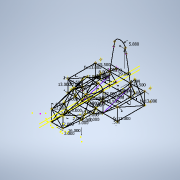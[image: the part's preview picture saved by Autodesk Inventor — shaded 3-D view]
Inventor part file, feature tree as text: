
AUTODESK INVENTOR PART (.ipt)
format: ipt  version: 2021 (Build 250183000, 183)  size: 271,872 bytes
history: native  units: in
note: dims shown in document units (in); Inventor stores cm internally (conversion verified against a paired STEP export)
features: other x52, plane x41, sketch x29
ambient origin geometry x8: Origin, YZ Plane, XZ Plane, XY Plane, X Axis, Y Axis, Z Axis, Center Point
feature tree (122):
  sketch  "Sketch1"  dims[d0=12.0in]
  plane  "Work Plane1"
  sketch  "Sketch2"  dims[d1=12.0in]
  plane  "Work Plane2"
  plane  "Work Plane3"
  sketch  "Sketch3"  dims[d2=2.0in]
  plane  "Work Plane4"
  sketch  "Sketch4"  dims[d3=-18.5in]
  plane  "Work Plane5"
  plane  "Work Plane6"
  plane  "Work Plane7"
  plane  "Work Plane8"
  plane  "Work Plane9"
  other  "Work Point1"
  other  "Work Point2"
  other  "Work Point3"
  other  "Work Point4"
  other  "Work Point5"
  other  "Work Point6"
  other  "Work Point7"
  other  "Work Point8"
  other  "Work Point9"
  other  "Work Point10"
  other  "Work Point11"
  other  "Work Point12"
  other  "Work Point13"
  other  "Work Point14"
  other  "Work Point15"
  other  "Work Point16"
  other  "Work Point17"
  other  "Work Point18"
  other  "Work Point19"
  other  "Work Point20"
  other  "Work Point21"
  other  "Work Point22"
  other  "Work Point23"
  other  "Work Point24"
  other  "Work Point25"
  other  "Work Point26"
  other  "Work Point27"
  other  "Work Point28"
  other  "Work Point29"
  other  "Work Point30"
  other  "Work Point31"
  other  "Work Point32"
  other  "Work Point33"
  other  "Work Point34"
  other  "Work Point35"
  other  "Work Point36"
  other  "Work Point37"
  other  "Work Point38"
  other  "Work Point39"
  other  "Work Point40"
  other  "Work Point41"
  other  "Work Point42"
  other  "Work Point43"
  other  "Work Point44"
  plane  "Work Plane10"
  sketch  "Sketch11"  dims[d4=16.0in]
  plane  "Work Plane11"
  sketch  "Sketch12"  dims[d5=2.0in]
  plane  "Work Plane12"
  sketch  "Sketch13"  dims[d6=3.0in]
  plane  "Work Plane13"
  sketch  "Sketch14"  dims[d7=6.0in]
  plane  "Work Plane14"
  sketch  "Sketch15"  dims[d8=3.0in]
  plane  "Work Plane15"
  sketch  "Sketch16"  dims[d9=6.0in]
  plane  "Work Plane16"
  sketch  "Sketch17"  dims[d10=-6.0in d11=-6.0in]
  plane  "Work Plane17"
  sketch  "Sketch18"  dims[d12=16.0in]
  other  "Work Point55"
  other  "Work Point56"
  other  "Work Point57"
  other  "Work Point58"
  plane  "Work Plane18"
  sketch  "Sketch19"  dims[d13=2.0in]
  plane  "Work Plane19"
  sketch  "Sketch20"  dims[d14=3.0in]
  plane  "Work Plane20"
  sketch  "Sketch21"  dims[d15=3.0in]
  plane  "Work Plane21"
  sketch  "Sketch22"  dims[d16=6.0in]
  plane  "Work Plane22"
  sketch  "Sketch23"  dims[d17=6.0in]
  plane  "Work Plane23"
  sketch  "Sketch24"  dims[d18=-7.5in]
  plane  "Work Plane24"
  sketch  "Sketch25"  dims[d19=22.0in]
  plane  "Work Plane25"
  sketch  "Sketch26"  dims[d21=20.0in]
  plane  "Work Plane26"
  sketch  "Sketch27"  dims[d23=12.0in]
  plane  "Work Plane27"
  sketch  "Sketch28"  dims[d24=25.0in]
  plane  "Work Plane28"
  sketch  "Sketch29"  dims[d25=13.0in]
  plane  "Work Plane29"
  plane  "Work Plane30"
  plane  "Work Plane31"
  plane  "Work Plane36"
  plane  "Work Plane37"
  plane  "Work Plane39"
  plane  "Work Plane53"
  sketch  "Sketch41"  dims[d26=13.0in]
  plane  "Work Plane41"
  sketch  "Sketch42"  dims[d27=13.0in]
  plane  "Work Plane42"
  sketch  "Sketch43"  dims[d28=13.0in]
  plane  "Work Plane43"
  plane  "Work Plane44"
  other  "Work Point63"
  other  "Work Point64"
  other  "Work Point65"
  other  "Work Point66"
  plane  "Work Plane50"
  sketch  "Sketch51"  dims[d29=15.5in]
  plane  "Work Plane51"
  sketch  "Sketch52"  dims[d30=15.5in d31=-29.4in d32=22.0in d33=13.0in d34=13.0in d35=13.0in d36=13.0in d37=15.5in d38=15.5in d42=5.88in d43=29.0in d45=-6.0in d52=-7.5in d58=-6.0in d61=-6.0in d67=9.8in d68=9.8in d69=22.0in d72=29.4in d74=29.4in d85=7.0in d105=4.299in d109=0.0831in d110=8.0in d113=8.0in d114=4.299in d116=0.0831in d117=0.5in d118=0.5in]
  sketch  "3D Sketch1"
